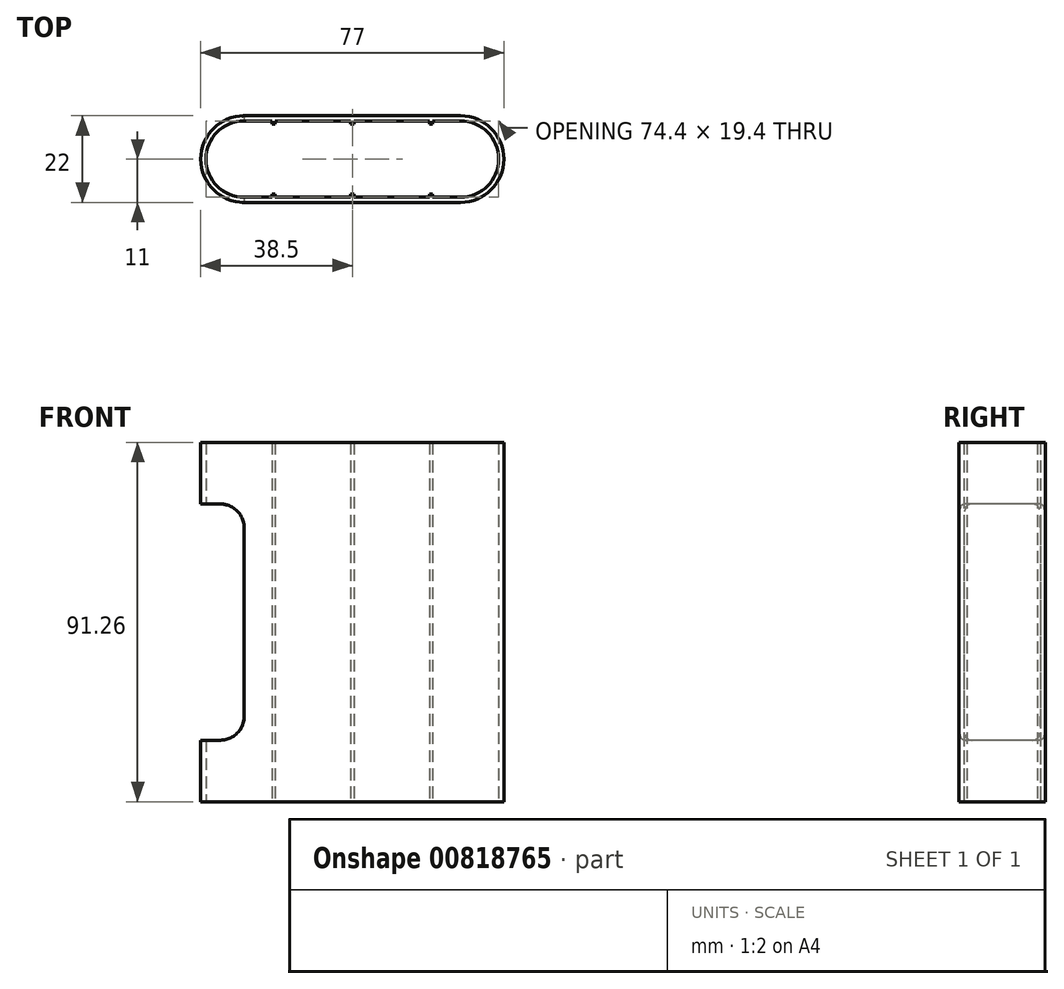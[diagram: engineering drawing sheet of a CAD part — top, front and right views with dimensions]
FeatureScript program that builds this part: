
annotation { "Feature Type Name" : "Feature", "Feature Type Description" : "" }
export const myFeature = defineFeature(function(context is Context, id is Id, definition is map)
    precondition{}
    {
        {
            var Q0;
            Q0=qCreatedBy(makeId("Top.planeOp"),FACE);
            var sketch = newSketch(context, id + "F0", { "sketchPlane" : qUnion([Q0])});
            skLineSegment(sketch, "E0", {"start": v(-38.5, 0) * mm, "end": v(38.5, 0) * mm, "construction": true});
            skLineSegment(sketch, "E1", {"start": v(-38.5, 0) * mm, "end": v(-38.5, 0) * mm});
            skLineSegment(sketch, "E2", {"start": v(-27.5, 11) * mm, "end": v(27.5, 11) * mm});
            skLineSegment(sketch, "E3", {"start": v(38.5, 0) * mm, "end": v(38.5, 0) * mm});
            skPoint(sketch, "E4.visualSharp", {"position": v(-38.5, 11) * mm});
            skArc(sketch, "E4.filletArc", {"start": v(-27.5, 11) * mm, "mid": v(-35.28, 7.78) * mm, "end": v(-38.5, 0) * mm});
            skPoint(sketch, "E5.visualSharp", {"position": v(38.5, 11) * mm});
            skArc(sketch, "E5.filletArc", {"start": v(38.5, 0) * mm, "mid": v(35.28, 7.78) * mm, "end": v(27.5, 11) * mm});
            skArc(sketch, "E6.0", {"start": v(-27.5, 9.7) * mm, "mid": v(-34.36, 6.86) * mm, "end": v(-37.2, 0) * mm});
            skLineSegment(sketch, "E6.1", {"start": v(-27.5, 9.7) * mm, "end": v(-20.4, 9.7) * mm});
            skArc(sketch, "E6.2", {"start": v(37.2, 0) * mm, "mid": v(34.36, 6.86) * mm, "end": v(27.5, 9.7) * mm});
            skLineSegment(sketch, "E7", {"start": v(0, 9.7) * mm, "end": v(0, 8.9) * mm, "construction": true});
            skLineSegment(sketch, "E8.trimOffspring", {"start": v(0.4, 9.7) * mm, "end": v(19.6, 9.7) * mm});
            skLineSegment(sketch, "E9", {"start": v(-20, 9.7) * mm, "end": v(-20, 8.9) * mm, "construction": true});
            skLineSegment(sketch, "E10", {"start": v(-20.4, 9.7) * mm, "end": v(-20.4, 8.9) * mm});
            skLineSegment(sketch, "E11.MirrorCS", {"start": v(-19.6, 9.7) * mm, "end": v(-19.6, 8.9) * mm});
            skLineSegment(sketch, "E12.trimOffspring", {"start": v(-19.6, 9.7) * mm, "end": v(-0.4, 9.7) * mm});
            skLineSegment(sketch, "E13.trimOffspring", {"start": v(20.4, 9.7) * mm, "end": v(27.5, 9.7) * mm});
            skLineSegment(sketch, "E14", {"start": v(-0.4, 9.7) * mm, "end": v(-0.4, 8.9) * mm});
            skLineSegment(sketch, "E15.MirrorCS", {"start": v(0.4, 9.7) * mm, "end": v(0.4, 8.9) * mm});
            skLineSegment(sketch, "E16", {"start": v(-0.4, 8.9) * mm, "end": v(0.4, 8.9) * mm});
            skLineSegment(sketch, "E17", {"start": v(-20.4, 8.9) * mm, "end": v(-19.6, 8.9) * mm});
            skLineSegment(sketch, "E18.MirrorCS", {"start": v(20.4, 9.7) * mm, "end": v(20.4, 8.9) * mm});
            skLineSegment(sketch, "E19.MirrorCS", {"start": v(19.6, 9.7) * mm, "end": v(19.6, 8.9) * mm});
            skLineSegment(sketch, "E20.MirrorCS", {"start": v(20.4, 8.9) * mm, "end": v(19.6, 8.9) * mm});
            skLineSegment(sketch, "E21.MirrorCS", {"start": v(-27.5, -11) * mm, "end": v(27.5, -11) * mm});
            skArc(sketch, "E22.MirrorCS", {"start": v(-27.5, -11) * mm, "mid": v(-35.28, -7.78) * mm, "end": v(-38.5, 0) * mm});
            skArc(sketch, "E23.MirrorCS", {"start": v(-27.5, -9.7) * mm, "mid": v(-34.36, -6.86) * mm, "end": v(-37.2, 0) * mm});
            skLineSegment(sketch, "E24.MirrorCS", {"start": v(-27.5, -9.7) * mm, "end": v(-20.4, -9.7) * mm});
            skLineSegment(sketch, "E25.MirrorCS", {"start": v(-19.6, -9.7) * mm, "end": v(-0.4, -9.7) * mm});
            skLineSegment(sketch, "E26.MirrorCS", {"start": v(-19.6, -9.7) * mm, "end": v(-19.6, -8.9) * mm});
            skLineSegment(sketch, "E27.MirrorCS", {"start": v(-20.4, -9.7) * mm, "end": v(-20.4, -8.9) * mm});
            skLineSegment(sketch, "E28.MirrorCS", {"start": v(-20.4, -8.9) * mm, "end": v(-19.6, -8.9) * mm});
            skLineSegment(sketch, "E29.MirrorCS", {"start": v(0.4, -9.7) * mm, "end": v(0.4, -8.9) * mm});
            skLineSegment(sketch, "E30.MirrorCS", {"start": v(-0.4, -9.7) * mm, "end": v(-0.4, -8.9) * mm});
            skLineSegment(sketch, "E31.MirrorCS", {"start": v(-0.4, -8.9) * mm, "end": v(0.4, -8.9) * mm});
            skLineSegment(sketch, "E32.MirrorCS", {"start": v(0.4, -9.7) * mm, "end": v(19.6, -9.7) * mm});
            skLineSegment(sketch, "E33.MirrorCS", {"start": v(19.6, -9.7) * mm, "end": v(19.6, -8.9) * mm});
            skLineSegment(sketch, "E34.MirrorCS", {"start": v(20.4, -8.9) * mm, "end": v(19.6, -8.9) * mm});
            skLineSegment(sketch, "E35.MirrorCS", {"start": v(20.4, -9.7) * mm, "end": v(20.4, -8.9) * mm});
            skLineSegment(sketch, "E36.MirrorCS", {"start": v(20.4, -9.7) * mm, "end": v(27.5, -9.7) * mm});
            skArc(sketch, "E37.MirrorCS", {"start": v(37.2, 0) * mm, "mid": v(34.36, -6.86) * mm, "end": v(27.5, -9.7) * mm});
            skArc(sketch, "E38.MirrorCS", {"start": v(38.5, 0) * mm, "mid": v(35.28, -7.78) * mm, "end": v(27.5, -11) * mm});
            skSolve(sketch);
        }
        {
            var Q0;
            Q0=makeQuery(id+"F0.imprint","IMPRINT",FACE,{"disambiguationData":[TD([[makeQuery(id+"F0.imprint","IMPRINT",EDGE,{"derivedFrom":sQuery(id+"F0.wireOp",EDGE,"E2")}),-1.0]])]});
            extrude(context, id + "F1", {"entities" : qUnion([Q0]), "endBound" : BoundingType.SYMMETRIC, "depth" : 91.25 * mm, "offsetDistance" : 25 * mm});
        }
        {
            var Q0;
            Q0=qCreatedBy(makeId("Front.planeOp"),FACE);
            var sketch = newSketch(context, id + "F2", { "sketchPlane" : qUnion([Q0])});
            skLineSegment(sketch, "E39", {"start": v(0, 46) * mm, "end": v(0, -46) * mm, "construction": true});
            skLineSegment(sketch, "E40.bottom", {"start": v(-33.5, 30) * mm, "end": v(-38.5, 30) * mm});
            skLineSegment(sketch, "E40.top", {"start": v(-33.5, -30) * mm, "end": v(-38.5, -30) * mm});
            skLineSegment(sketch, "E40.left", {"start": v(-27.5, 24) * mm, "end": v(-27.5, -24) * mm});
            skLineSegment(sketch, "E40.right", {"start": v(-38.5, 30) * mm, "end": v(-38.5, -30) * mm});
            skLineSegment(sketch, "E41", {"start": v(-27.5, 0) * mm, "end": v(0, 0) * mm, "construction": true});
            skPoint(sketch, "E42.visualSharp", {"position": v(-27.5, 30) * mm});
            skArc(sketch, "E42.filletArc", {"start": v(-27.5, 24) * mm, "mid": v(-29.26, 28.24) * mm, "end": v(-33.5, 30) * mm});
            skPoint(sketch, "E43.visualSharp", {"position": v(-27.5, -30) * mm});
            skArc(sketch, "E43.filletArc", {"start": v(-33.5, -30) * mm, "mid": v(-29.26, -28.24) * mm, "end": v(-27.5, -24) * mm});
            skArc(sketch, "E44.MirrorCS", {"start": v(27.5, 24) * mm, "mid": v(29.26, 28.24) * mm, "end": v(33.5, 30) * mm});
            skArc(sketch, "E45.MirrorCS", {"start": v(33.5, -30) * mm, "mid": v(29.26, -28.24) * mm, "end": v(27.5, -24) * mm});
            skLineSegment(sketch, "E46.MirrorCS", {"start": v(27.5, 24) * mm, "end": v(27.5, -24) * mm});
            skLineSegment(sketch, "E47.MirrorCS", {"start": v(38.5, 30) * mm, "end": v(38.5, -30) * mm});
            skLineSegment(sketch, "E48.MirrorCS", {"start": v(33.5, 30) * mm, "end": v(38.5, 30) * mm});
            skLineSegment(sketch, "E49.MirrorCS", {"start": v(33.5, -30) * mm, "end": v(38.5, -30) * mm});
            skSolve(sketch);
        }
        {
            var Q0;
            Q0=makeQuery(id+"F2.imprint","IMPRINT",FACE,{"disambiguationData":[TD([[makeQuery(id+"F2.imprint","IMPRINT",EDGE,{"derivedFrom":sQuery(id+"F2.wireOp",EDGE,"E40.left")}),-1.0]])]});
            var Q1;
            Q1=makeQuery(id+"F2.imprint","IMPRINT",FACE,{"disambiguationData":[TD([[makeQuery(id+"F2.imprint","IMPRINT",EDGE,{"derivedFrom":sQuery(id+"F2.wireOp",EDGE,"E44.MirrorCS")}),-1.0]])]});
            extrude(context, id + "F3", {"entities" : qUnion([Q0, Q1]), "operationType" : NewBodyOperationType.REMOVE, "endBound" : BoundingType.SYMMETRIC, "oppositeDirection" : true, "depth" : 25 * mm, "offsetDistance" : 25 * mm});
        }
    });
